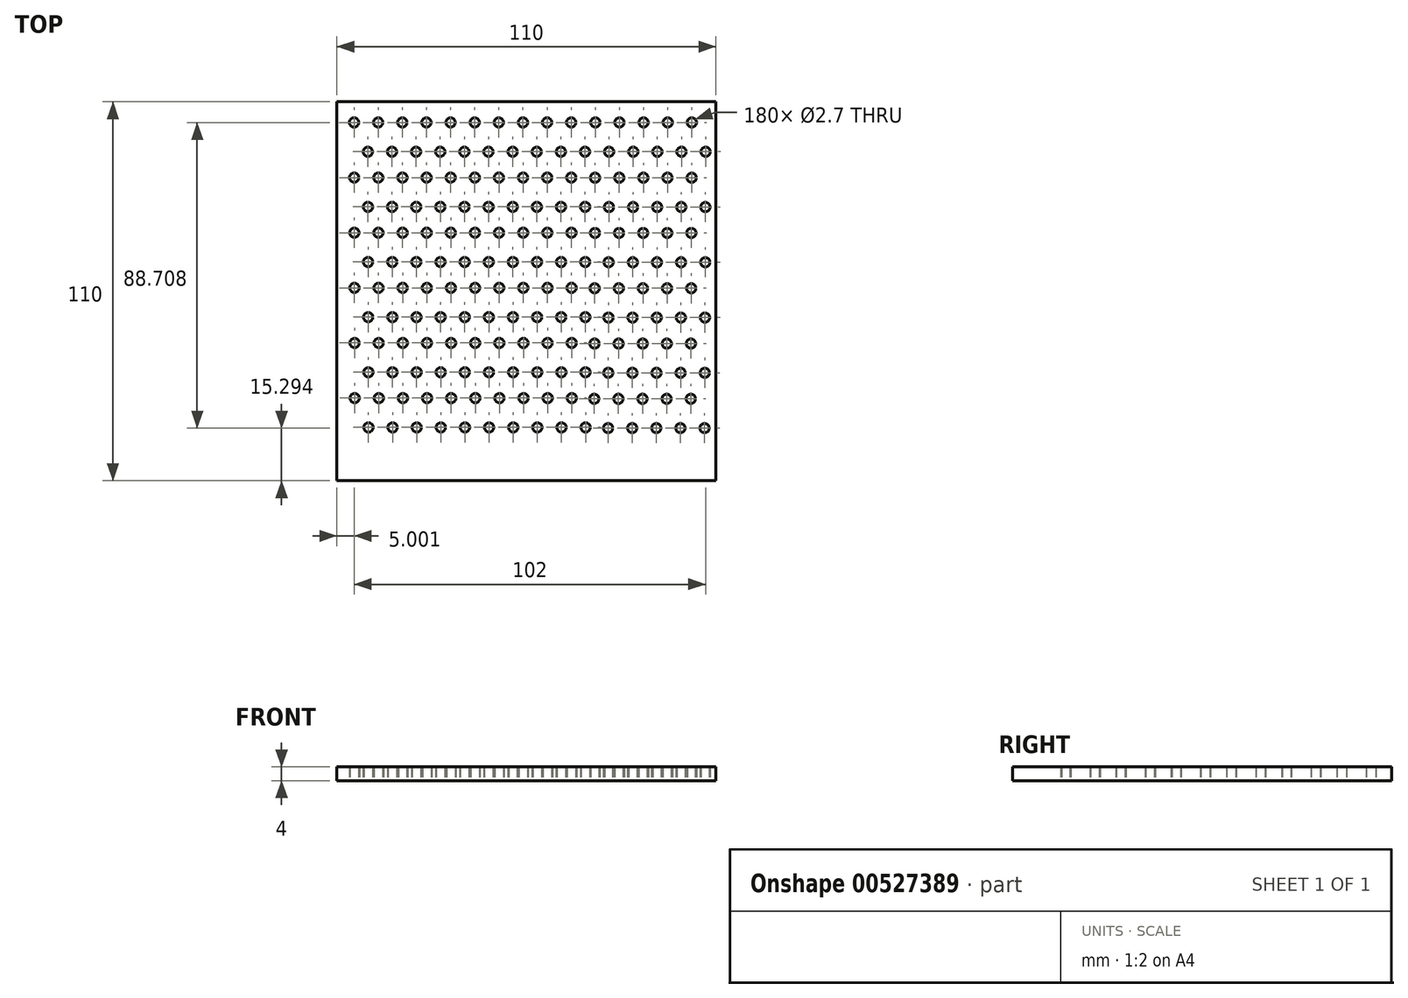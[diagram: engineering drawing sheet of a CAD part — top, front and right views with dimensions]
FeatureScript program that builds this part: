
annotation { "Feature Type Name" : "Feature", "Feature Type Description" : "" }
export const myFeature = defineFeature(function(context is Context, id is Id, definition is map)
    precondition{}
    {
        {
            var Q0;
            Q0=qCreatedBy(makeId("Top.planeOp"),FACE);
            var sketch = newSketch(context, id + "F0", { "sketchPlane" : qUnion([Q0])});
            skLineSegment(sketch, "E0.bottom", {"start": v(-73.94, -2.16) * mm, "end": v(36.06, -2.16) * mm});
            skLineSegment(sketch, "E0.top", {"start": v(-73.94, -112.16) * mm, "end": v(36.06, -112.16) * mm});
            skLineSegment(sketch, "E0.left", {"start": v(-73.94, -2.16) * mm, "end": v(-73.94, -112.16) * mm});
            skLineSegment(sketch, "E0.right", {"start": v(36.06, -2.16) * mm, "end": v(36.06, -112.16) * mm});
            skCircle(sketch, "E1", {"center": v(-68.94, -8.16) * mm, "radius": 1.35 * mm});
            skCircle(sketch, "E2", {"center": v(-64.94, -16.66) * mm, "radius": 1.35 * mm});
            skCircle(sketch, "E3.1.0.0", {"center": v(-57.94, -16.66) * mm, "radius": 1.35 * mm});
            skCircle(sketch, "E3.1.0.1", {"center": v(-61.94, -8.16) * mm, "radius": 1.35 * mm});
            skCircle(sketch, "E3.2.0.0", {"center": v(-50.94, -16.66) * mm, "radius": 1.35 * mm});
            skCircle(sketch, "E3.2.0.1", {"center": v(-54.94, -8.16) * mm, "radius": 1.35 * mm});
            skCircle(sketch, "E3.3.0.0", {"center": v(-43.94, -16.66) * mm, "radius": 1.35 * mm});
            skCircle(sketch, "E3.3.0.1", {"center": v(-47.94, -8.16) * mm, "radius": 1.35 * mm});
            skCircle(sketch, "E3.4.0.0", {"center": v(-36.94, -16.66) * mm, "radius": 1.35 * mm});
            skCircle(sketch, "E3.4.0.1", {"center": v(-40.94, -8.16) * mm, "radius": 1.35 * mm});
            skCircle(sketch, "E3.5.0.0", {"center": v(-29.94, -16.66) * mm, "radius": 1.35 * mm});
            skCircle(sketch, "E3.5.0.1", {"center": v(-33.94, -8.16) * mm, "radius": 1.35 * mm});
            skCircle(sketch, "E3.6.0.0", {"center": v(-22.94, -16.66) * mm, "radius": 1.35 * mm});
            skCircle(sketch, "E3.6.0.1", {"center": v(-26.94, -8.16) * mm, "radius": 1.35 * mm});
            skCircle(sketch, "E3.7.0.0", {"center": v(-15.94, -16.66) * mm, "radius": 1.35 * mm});
            skCircle(sketch, "E3.7.0.1", {"center": v(-19.94, -8.16) * mm, "radius": 1.35 * mm});
            skCircle(sketch, "E3.8.0.0", {"center": v(-8.94, -16.66) * mm, "radius": 1.35 * mm});
            skCircle(sketch, "E3.8.0.1", {"center": v(-12.94, -8.16) * mm, "radius": 1.35 * mm});
            skCircle(sketch, "E3.9.0.0", {"center": v(-1.94, -16.66) * mm, "radius": 1.35 * mm});
            skCircle(sketch, "E3.9.0.1", {"center": v(-5.94, -8.16) * mm, "radius": 1.35 * mm});
            skLineSegment(sketch, "E3.direction1", {"start": v(-64.94, -16.66) * mm, "end": v(-57.94, -16.66) * mm, "construction": true});
            skCircle(sketch, "E4.1.0.0", {"center": v(-15.9, -32.66) * mm, "radius": 1.35 * mm});
            skCircle(sketch, "E4.1.0.1", {"center": v(-19.9, -24.16) * mm, "radius": 1.35 * mm});
            skCircle(sketch, "E4.1.0.2", {"center": v(-22.9, -32.66) * mm, "radius": 1.35 * mm});
            skCircle(sketch, "E4.1.0.3", {"center": v(-64.9, -32.66) * mm, "radius": 1.35 * mm});
            skLineSegment(sketch, "E4.1.0.4", {"start": v(-64.9, -32.66) * mm, "end": v(-57.9, -32.66) * mm, "construction": true});
            skCircle(sketch, "E4.1.0.5", {"center": v(-5.9, -24.16) * mm, "radius": 1.35 * mm});
            skCircle(sketch, "E4.1.0.6", {"center": v(-50.9, -32.66) * mm, "radius": 1.35 * mm});
            skCircle(sketch, "E4.1.0.7", {"center": v(-40.9, -24.16) * mm, "radius": 1.35 * mm});
            skCircle(sketch, "E4.1.0.8", {"center": v(-12.9, -24.16) * mm, "radius": 1.35 * mm});
            skCircle(sketch, "E4.1.0.9", {"center": v(-29.9, -32.66) * mm, "radius": 1.35 * mm});
            skCircle(sketch, "E4.1.0.10", {"center": v(-43.9, -32.66) * mm, "radius": 1.35 * mm});
            skCircle(sketch, "E4.1.0.11", {"center": v(-54.9, -24.16) * mm, "radius": 1.35 * mm});
            skCircle(sketch, "E4.1.0.12", {"center": v(-61.9, -24.16) * mm, "radius": 1.35 * mm});
            skCircle(sketch, "E4.1.0.13", {"center": v(-36.9, -32.66) * mm, "radius": 1.35 * mm});
            skCircle(sketch, "E4.1.0.14", {"center": v(-8.9, -32.66) * mm, "radius": 1.35 * mm});
            skCircle(sketch, "E4.1.0.15", {"center": v(-26.9, -24.16) * mm, "radius": 1.35 * mm});
            skCircle(sketch, "E4.1.0.16", {"center": v(-1.9, -32.66) * mm, "radius": 1.35 * mm});
            skCircle(sketch, "E4.1.0.17", {"center": v(-47.9, -24.16) * mm, "radius": 1.35 * mm});
            skCircle(sketch, "E4.1.0.18", {"center": v(-33.9, -24.16) * mm, "radius": 1.35 * mm});
            skCircle(sketch, "E4.1.0.19", {"center": v(-57.9, -32.66) * mm, "radius": 1.35 * mm});
            skCircle(sketch, "E4.1.0.20", {"center": v(-68.9, -24.16) * mm, "radius": 1.35 * mm});
            skCircle(sketch, "E4.2.0.0", {"center": v(-15.87, -48.66) * mm, "radius": 1.35 * mm});
            skCircle(sketch, "E4.2.0.1", {"center": v(-19.87, -40.16) * mm, "radius": 1.35 * mm});
            skCircle(sketch, "E4.2.0.2", {"center": v(-22.87, -48.66) * mm, "radius": 1.35 * mm});
            skCircle(sketch, "E4.2.0.3", {"center": v(-64.87, -48.66) * mm, "radius": 1.35 * mm});
            skLineSegment(sketch, "E4.2.0.4", {"start": v(-64.87, -48.66) * mm, "end": v(-57.87, -48.66) * mm, "construction": true});
            skCircle(sketch, "E4.2.0.5", {"center": v(-5.87, -40.16) * mm, "radius": 1.35 * mm});
            skCircle(sketch, "E4.2.0.6", {"center": v(-50.87, -48.66) * mm, "radius": 1.35 * mm});
            skCircle(sketch, "E4.2.0.7", {"center": v(-40.87, -40.16) * mm, "radius": 1.35 * mm});
            skCircle(sketch, "E4.2.0.8", {"center": v(-12.87, -40.16) * mm, "radius": 1.35 * mm});
            skCircle(sketch, "E4.2.0.9", {"center": v(-29.87, -48.66) * mm, "radius": 1.35 * mm});
            skCircle(sketch, "E4.2.0.10", {"center": v(-43.87, -48.66) * mm, "radius": 1.35 * mm});
            skCircle(sketch, "E4.2.0.11", {"center": v(-54.87, -40.16) * mm, "radius": 1.35 * mm});
            skCircle(sketch, "E4.2.0.12", {"center": v(-61.87, -40.16) * mm, "radius": 1.35 * mm});
            skCircle(sketch, "E4.2.0.13", {"center": v(-36.87, -48.66) * mm, "radius": 1.35 * mm});
            skCircle(sketch, "E4.2.0.14", {"center": v(-8.87, -48.66) * mm, "radius": 1.35 * mm});
            skCircle(sketch, "E4.2.0.15", {"center": v(-26.87, -40.16) * mm, "radius": 1.35 * mm});
            skCircle(sketch, "E4.2.0.16", {"center": v(-1.87, -48.66) * mm, "radius": 1.35 * mm});
            skCircle(sketch, "E4.2.0.17", {"center": v(-47.87, -40.16) * mm, "radius": 1.35 * mm});
            skCircle(sketch, "E4.2.0.18", {"center": v(-33.87, -40.16) * mm, "radius": 1.35 * mm});
            skCircle(sketch, "E4.2.0.19", {"center": v(-57.87, -48.66) * mm, "radius": 1.35 * mm});
            skCircle(sketch, "E4.2.0.20", {"center": v(-68.87, -40.16) * mm, "radius": 1.35 * mm});
            skCircle(sketch, "E4.3.0.0", {"center": v(-15.83, -64.66) * mm, "radius": 1.35 * mm});
            skCircle(sketch, "E4.3.0.1", {"center": v(-19.83, -56.16) * mm, "radius": 1.35 * mm});
            skCircle(sketch, "E4.3.0.2", {"center": v(-22.83, -64.66) * mm, "radius": 1.35 * mm});
            skCircle(sketch, "E4.3.0.3", {"center": v(-64.83, -64.66) * mm, "radius": 1.35 * mm});
            skLineSegment(sketch, "E4.3.0.4", {"start": v(-64.83, -64.66) * mm, "end": v(-57.83, -64.66) * mm, "construction": true});
            skCircle(sketch, "E4.3.0.5", {"center": v(-5.83, -56.16) * mm, "radius": 1.35 * mm});
            skCircle(sketch, "E4.3.0.6", {"center": v(-50.83, -64.66) * mm, "radius": 1.35 * mm});
            skCircle(sketch, "E4.3.0.7", {"center": v(-40.83, -56.16) * mm, "radius": 1.35 * mm});
            skCircle(sketch, "E4.3.0.8", {"center": v(-12.83, -56.16) * mm, "radius": 1.35 * mm});
            skCircle(sketch, "E4.3.0.9", {"center": v(-29.83, -64.66) * mm, "radius": 1.35 * mm});
            skCircle(sketch, "E4.3.0.10", {"center": v(-43.83, -64.66) * mm, "radius": 1.35 * mm});
            skCircle(sketch, "E4.3.0.11", {"center": v(-54.83, -56.16) * mm, "radius": 1.35 * mm});
            skCircle(sketch, "E4.3.0.12", {"center": v(-61.83, -56.16) * mm, "radius": 1.35 * mm});
            skCircle(sketch, "E4.3.0.13", {"center": v(-36.83, -64.66) * mm, "radius": 1.35 * mm});
            skCircle(sketch, "E4.3.0.14", {"center": v(-8.83, -64.66) * mm, "radius": 1.35 * mm});
            skCircle(sketch, "E4.3.0.15", {"center": v(-26.83, -56.16) * mm, "radius": 1.35 * mm});
            skCircle(sketch, "E4.3.0.16", {"center": v(-1.83, -64.66) * mm, "radius": 1.35 * mm});
            skCircle(sketch, "E4.3.0.17", {"center": v(-47.83, -56.16) * mm, "radius": 1.35 * mm});
            skCircle(sketch, "E4.3.0.18", {"center": v(-33.83, -56.16) * mm, "radius": 1.35 * mm});
            skCircle(sketch, "E4.3.0.19", {"center": v(-57.83, -64.66) * mm, "radius": 1.35 * mm});
            skCircle(sketch, "E4.3.0.20", {"center": v(-68.83, -56.16) * mm, "radius": 1.35 * mm});
            skCircle(sketch, "E4.4.0.0", {"center": v(-15.8, -80.66) * mm, "radius": 1.35 * mm});
            skCircle(sketch, "E4.4.0.1", {"center": v(-19.8, -72.16) * mm, "radius": 1.35 * mm});
            skCircle(sketch, "E4.4.0.2", {"center": v(-22.8, -80.66) * mm, "radius": 1.35 * mm});
            skCircle(sketch, "E4.4.0.3", {"center": v(-64.8, -80.66) * mm, "radius": 1.35 * mm});
            skLineSegment(sketch, "E4.4.0.4", {"start": v(-64.8, -80.66) * mm, "end": v(-57.8, -80.66) * mm, "construction": true});
            skCircle(sketch, "E4.4.0.5", {"center": v(-5.8, -72.16) * mm, "radius": 1.35 * mm});
            skCircle(sketch, "E4.4.0.6", {"center": v(-50.8, -80.66) * mm, "radius": 1.35 * mm});
            skCircle(sketch, "E4.4.0.7", {"center": v(-40.8, -72.16) * mm, "radius": 1.35 * mm});
            skCircle(sketch, "E4.4.0.8", {"center": v(-12.8, -72.16) * mm, "radius": 1.35 * mm});
            skCircle(sketch, "E4.4.0.9", {"center": v(-29.8, -80.66) * mm, "radius": 1.35 * mm});
            skCircle(sketch, "E4.4.0.10", {"center": v(-43.8, -80.66) * mm, "radius": 1.35 * mm});
            skCircle(sketch, "E4.4.0.11", {"center": v(-54.8, -72.16) * mm, "radius": 1.35 * mm});
            skCircle(sketch, "E4.4.0.12", {"center": v(-61.8, -72.16) * mm, "radius": 1.35 * mm});
            skCircle(sketch, "E4.4.0.13", {"center": v(-36.8, -80.66) * mm, "radius": 1.35 * mm});
            skCircle(sketch, "E4.4.0.14", {"center": v(-8.8, -80.66) * mm, "radius": 1.35 * mm});
            skCircle(sketch, "E4.4.0.15", {"center": v(-26.8, -72.16) * mm, "radius": 1.35 * mm});
            skCircle(sketch, "E4.4.0.16", {"center": v(-1.8, -80.66) * mm, "radius": 1.35 * mm});
            skCircle(sketch, "E4.4.0.17", {"center": v(-47.8, -72.16) * mm, "radius": 1.35 * mm});
            skCircle(sketch, "E4.4.0.18", {"center": v(-33.8, -72.16) * mm, "radius": 1.35 * mm});
            skCircle(sketch, "E4.4.0.19", {"center": v(-57.8, -80.66) * mm, "radius": 1.35 * mm});
            skCircle(sketch, "E4.4.0.20", {"center": v(-68.8, -72.16) * mm, "radius": 1.35 * mm});
            skLineSegment(sketch, "E4.direction1", {"start": v(-64.94, -16.66) * mm, "end": v(-64.9, -32.66) * mm, "construction": true});
            skCircle(sketch, "E5.0.10.0", {"center": v(5.06, -16.66) * mm, "radius": 1.35 * mm});
            skCircle(sketch, "E5.2.10.0", {"center": v(1.06, -8.16) * mm, "radius": 1.35 * mm});
            skCircle(sketch, "E5.0.11.0", {"center": v(12.06, -16.66) * mm, "radius": 1.35 * mm});
            skCircle(sketch, "E5.2.11.0", {"center": v(8.06, -8.16) * mm, "radius": 1.35 * mm});
            skCircle(sketch, "E5.0.12.0", {"center": v(19.06, -16.66) * mm, "radius": 1.35 * mm});
            skCircle(sketch, "E5.2.12.0", {"center": v(15.06, -8.16) * mm, "radius": 1.35 * mm});
            skCircle(sketch, "E5.0.13.0", {"center": v(26.06, -16.66) * mm, "radius": 1.35 * mm});
            skCircle(sketch, "E5.2.13.0", {"center": v(22.06, -8.16) * mm, "radius": 1.35 * mm});
            skCircle(sketch, "E5.0.14.0", {"center": v(33.06, -16.66) * mm, "radius": 1.35 * mm});
            skCircle(sketch, "E5.2.14.0", {"center": v(29.06, -8.16) * mm, "radius": 1.35 * mm});
            skCircle(sketch, "E6.0.5.0", {"center": v(-15.76, -96.66) * mm, "radius": 1.35 * mm});
            skCircle(sketch, "E6.2.5.0", {"center": v(-19.76, -88.16) * mm, "radius": 1.35 * mm});
            skCircle(sketch, "E6.4.5.0", {"center": v(-22.76, -96.66) * mm, "radius": 1.35 * mm});
            skCircle(sketch, "E6.6.5.0", {"center": v(-64.76, -96.66) * mm, "radius": 1.35 * mm});
            skLineSegment(sketch, "E6.8.5.0", {"start": v(-64.76, -96.66) * mm, "end": v(-57.76, -96.66) * mm, "construction": true});
            skCircle(sketch, "E6.11.5.0", {"center": v(-5.76, -88.16) * mm, "radius": 1.35 * mm});
            skCircle(sketch, "E6.13.5.0", {"center": v(-50.76, -96.66) * mm, "radius": 1.35 * mm});
            skCircle(sketch, "E6.15.5.0", {"center": v(-40.76, -88.16) * mm, "radius": 1.35 * mm});
            skCircle(sketch, "E6.17.5.0", {"center": v(-12.76, -88.16) * mm, "radius": 1.35 * mm});
            skCircle(sketch, "E6.19.5.0", {"center": v(-29.76, -96.66) * mm, "radius": 1.35 * mm});
            skCircle(sketch, "E6.21.5.0", {"center": v(-43.76, -96.66) * mm, "radius": 1.35 * mm});
            skCircle(sketch, "E6.23.5.0", {"center": v(-54.76, -88.16) * mm, "radius": 1.35 * mm});
            skCircle(sketch, "E6.25.5.0", {"center": v(-61.76, -88.16) * mm, "radius": 1.35 * mm});
            skCircle(sketch, "E6.27.5.0", {"center": v(-36.76, -96.66) * mm, "radius": 1.35 * mm});
            skCircle(sketch, "E6.29.5.0", {"center": v(-8.76, -96.66) * mm, "radius": 1.35 * mm});
            skCircle(sketch, "E6.31.5.0", {"center": v(-26.76, -88.16) * mm, "radius": 1.35 * mm});
            skCircle(sketch, "E6.33.5.0", {"center": v(-1.76, -96.66) * mm, "radius": 1.35 * mm});
            skCircle(sketch, "E6.35.5.0", {"center": v(-47.76, -88.16) * mm, "radius": 1.35 * mm});
            skCircle(sketch, "E6.37.5.0", {"center": v(-33.76, -88.16) * mm, "radius": 1.35 * mm});
            skCircle(sketch, "E6.39.5.0", {"center": v(-57.76, -96.66) * mm, "radius": 1.35 * mm});
            skCircle(sketch, "E6.41.5.0", {"center": v(-68.76, -88.16) * mm, "radius": 1.35 * mm});
            skCircle(sketch, "E7.1.0.0", {"center": v(33, -32.7) * mm, "radius": 1.35 * mm});
            skCircle(sketch, "E7.1.0.1", {"center": v(26, -32.7) * mm, "radius": 1.35 * mm});
            skCircle(sketch, "E7.1.0.2", {"center": v(19, -32.7) * mm, "radius": 1.35 * mm});
            skCircle(sketch, "E7.1.0.3", {"center": v(1, -24.2) * mm, "radius": 1.35 * mm});
            skCircle(sketch, "E7.1.0.4", {"center": v(5, -32.7) * mm, "radius": 1.35 * mm});
            skCircle(sketch, "E7.1.0.5", {"center": v(12, -32.7) * mm, "radius": 1.35 * mm});
            skCircle(sketch, "E7.1.0.6", {"center": v(29, -24.2) * mm, "radius": 1.35 * mm});
            skCircle(sketch, "E7.1.0.7", {"center": v(22, -24.2) * mm, "radius": 1.35 * mm});
            skCircle(sketch, "E7.1.0.8", {"center": v(15, -24.2) * mm, "radius": 1.35 * mm});
            skCircle(sketch, "E7.1.0.9", {"center": v(8, -24.2) * mm, "radius": 1.35 * mm});
            skCircle(sketch, "E7.2.0.0", {"center": v(32.94, -48.74) * mm, "radius": 1.35 * mm});
            skCircle(sketch, "E7.2.0.1", {"center": v(25.94, -48.74) * mm, "radius": 1.35 * mm});
            skCircle(sketch, "E7.2.0.2", {"center": v(18.94, -48.74) * mm, "radius": 1.35 * mm});
            skCircle(sketch, "E7.2.0.3", {"center": v(0.94, -40.24) * mm, "radius": 1.35 * mm});
            skCircle(sketch, "E7.2.0.4", {"center": v(4.94, -48.74) * mm, "radius": 1.35 * mm});
            skCircle(sketch, "E7.2.0.5", {"center": v(11.94, -48.74) * mm, "radius": 1.35 * mm});
            skCircle(sketch, "E7.2.0.6", {"center": v(28.94, -40.24) * mm, "radius": 1.35 * mm});
            skCircle(sketch, "E7.2.0.7", {"center": v(21.94, -40.24) * mm, "radius": 1.35 * mm});
            skCircle(sketch, "E7.2.0.8", {"center": v(14.94, -40.24) * mm, "radius": 1.35 * mm});
            skCircle(sketch, "E7.2.0.9", {"center": v(7.94, -40.24) * mm, "radius": 1.35 * mm});
            skCircle(sketch, "E7.3.0.0", {"center": v(32.88, -64.78) * mm, "radius": 1.35 * mm});
            skCircle(sketch, "E7.3.0.1", {"center": v(25.88, -64.78) * mm, "radius": 1.35 * mm});
            skCircle(sketch, "E7.3.0.2", {"center": v(18.88, -64.78) * mm, "radius": 1.35 * mm});
            skCircle(sketch, "E7.3.0.3", {"center": v(0.88, -56.28) * mm, "radius": 1.35 * mm});
            skCircle(sketch, "E7.3.0.4", {"center": v(4.88, -64.78) * mm, "radius": 1.35 * mm});
            skCircle(sketch, "E7.3.0.5", {"center": v(11.88, -64.78) * mm, "radius": 1.35 * mm});
            skCircle(sketch, "E7.3.0.6", {"center": v(28.88, -56.28) * mm, "radius": 1.35 * mm});
            skCircle(sketch, "E7.3.0.7", {"center": v(21.88, -56.28) * mm, "radius": 1.35 * mm});
            skCircle(sketch, "E7.3.0.8", {"center": v(14.88, -56.28) * mm, "radius": 1.35 * mm});
            skCircle(sketch, "E7.3.0.9", {"center": v(7.88, -56.28) * mm, "radius": 1.35 * mm});
            skCircle(sketch, "E7.4.0.0", {"center": v(32.82, -80.82) * mm, "radius": 1.35 * mm});
            skCircle(sketch, "E7.4.0.1", {"center": v(25.82, -80.82) * mm, "radius": 1.35 * mm});
            skCircle(sketch, "E7.4.0.2", {"center": v(18.82, -80.82) * mm, "radius": 1.35 * mm});
            skCircle(sketch, "E7.4.0.3", {"center": v(0.82, -72.32) * mm, "radius": 1.35 * mm});
            skCircle(sketch, "E7.4.0.4", {"center": v(4.82, -80.82) * mm, "radius": 1.35 * mm});
            skCircle(sketch, "E7.4.0.5", {"center": v(11.82, -80.82) * mm, "radius": 1.35 * mm});
            skCircle(sketch, "E7.4.0.6", {"center": v(28.82, -72.32) * mm, "radius": 1.35 * mm});
            skCircle(sketch, "E7.4.0.7", {"center": v(21.82, -72.32) * mm, "radius": 1.35 * mm});
            skCircle(sketch, "E7.4.0.8", {"center": v(14.82, -72.32) * mm, "radius": 1.35 * mm});
            skCircle(sketch, "E7.4.0.9", {"center": v(7.82, -72.32) * mm, "radius": 1.35 * mm});
            skCircle(sketch, "E7.5.0.0", {"center": v(32.75, -96.87) * mm, "radius": 1.35 * mm});
            skCircle(sketch, "E7.5.0.1", {"center": v(25.75, -96.87) * mm, "radius": 1.35 * mm});
            skCircle(sketch, "E7.5.0.2", {"center": v(18.75, -96.87) * mm, "radius": 1.35 * mm});
            skCircle(sketch, "E7.5.0.3", {"center": v(0.75, -88.37) * mm, "radius": 1.35 * mm});
            skCircle(sketch, "E7.5.0.4", {"center": v(4.75, -96.87) * mm, "radius": 1.35 * mm});
            skCircle(sketch, "E7.5.0.5", {"center": v(11.75, -96.87) * mm, "radius": 1.35 * mm});
            skCircle(sketch, "E7.5.0.6", {"center": v(28.75, -88.37) * mm, "radius": 1.35 * mm});
            skCircle(sketch, "E7.5.0.7", {"center": v(21.75, -88.37) * mm, "radius": 1.35 * mm});
            skCircle(sketch, "E7.5.0.8", {"center": v(14.75, -88.37) * mm, "radius": 1.35 * mm});
            skCircle(sketch, "E7.5.0.9", {"center": v(7.75, -88.37) * mm, "radius": 1.35 * mm});
            skLineSegment(sketch, "E7.direction1", {"start": v(5.06, -16.66) * mm, "end": v(5, -32.7) * mm, "construction": true});
            skSolve(sketch);
        }
        {
            var Q0;
            Q0=makeQuery(id+"F0.imprint","IMPRINT",FACE,{"disambiguationData":[TD([[makeQuery(id+"F0.imprint","IMPRINT",EDGE,{"derivedFrom":sQuery(id+"F0.wireOp",EDGE,"E0.bottom")}),-1.0]])]});
            var Q1;
            Q1=makeQuery(id+"F0.imprint","IMPRINT",FACE,{"disambiguationData":[TD([[makeQuery(id+"F0.imprint","IMPRINT",EDGE,{"derivedFrom":sQuery(id+"F0.wireOp",EDGE,"3b7fb202-e533-49a3-9cd9-afe437150003")}),1.0]])]});
            var Q2;
            Q2=makeQuery(id+"F0.imprint","IMPRINT",FACE,{"disambiguationData":[TD([[makeQuery(id+"F0.imprint","IMPRINT",EDGE,{"derivedFrom":sQuery(id+"F0.wireOp",EDGE,"6183986e-af95-435e-b1a4-9535b91c72f9")}),1.0]])]});
            extrude(context, id + "F1", {"entities" : qUnion([Q0, Q1, Q2]), "depth" : 4 * mm, "offsetDistance" : 25 * mm});
        }
    });
